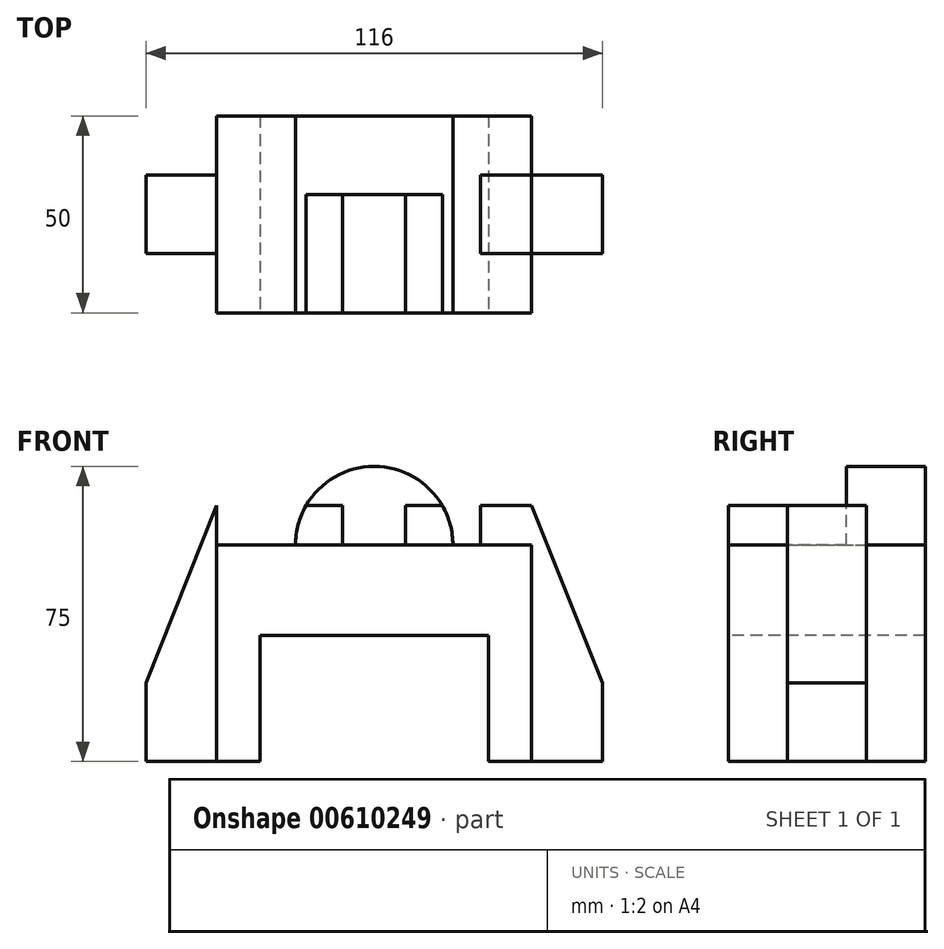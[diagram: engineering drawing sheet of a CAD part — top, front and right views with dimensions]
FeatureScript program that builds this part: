
annotation { "Feature Type Name" : "Feature", "Feature Type Description" : "" }
export const myFeature = defineFeature(function(context is Context, id is Id, definition is map)
    precondition{}
    {
        {
            var Q0;
            Q0=qCreatedBy(makeId("Top.planeOp"),FACE);
            var sketch = newSketch(context, id + "F0", { "sketchPlane" : qUnion([Q0])});
            skLineSegment(sketch, "E0.bottom", {"start": v(40, 25) * mm, "end": v(-40, 25) * mm});
            skLineSegment(sketch, "E0.top", {"start": v(40, -25) * mm, "end": v(-40, -25) * mm});
            skLineSegment(sketch, "E0.left", {"start": v(40, 25) * mm, "end": v(40, -25) * mm});
            skLineSegment(sketch, "E0.right", {"start": v(-40, 25) * mm, "end": v(-40, -25) * mm});
            skPoint(sketch, "E0.middle", {"position": v(0, 0) * mm});
            skSolve(sketch);
        }
        {
            var Q0;
            Q0 = qSketchRegion(id + "F0", true);
            extrude(context, id + "F1", {"entities" : qUnion([Q0]), "depth" : 55 * mm, "offsetDistance" : 25 * mm});
        }
        {
            var Q0;
            Q0=makeQuery(id+"F1.opExtrude","SWEPT_FACE",FACE,{"disambiguationData":[OSD([sQuery(id+"F0.wireOp",EDGE,"E0.top")])]});
            var sketch = newSketch(context, id + "F2", { "sketchPlane" : qUnion([Q0])});
            skLineSegment(sketch, "E1", {"start": v(-40, 0) * mm, "end": v(-29, 0) * mm});
            skLineSegment(sketch, "E2", {"start": v(40, 0) * mm, "end": v(29, 0) * mm});
            skLineSegment(sketch, "E3", {"start": v(29, 0) * mm, "end": v(29, 32) * mm});
            skLineSegment(sketch, "E4", {"start": v(29, 32) * mm, "end": v(-29, 32) * mm});
            skLineSegment(sketch, "E5", {"start": v(-29, 32) * mm, "end": v(-29, 0) * mm});
            skSolve(sketch);
        }
        {
            var Q0;
            {var subQ0=sQuery(id+"F2.wireOp",EDGE,"E3");Q0=makeQuery(id+"F2.imprint","IMPRINT",FACE,{"disambiguationData":[TD([[makeQuery(id+"F2.imprint","IMPRINT",EDGE,{"derivedFrom":subQ0}),1.0]])]});}
            extrude(context, id + "F3", {"entities" : qUnion([Q0]), "operationType" : NewBodyOperationType.REMOVE, "oppositeDirection" : true, "depth" : 114.9 * mm, "offsetDistance" : 25 * mm});
        }
        {
            var Q0;
            {var subQ0=sQuery(id+"F0.wireOp",EDGE,"E0.bottom");var subQ1=makeQuery(id+"F1.opExtrude","CAP_EDGE",EDGE,{"disambiguationData":[OSD([subQ0])],"isStart":false});Q0=makeQuery(id+"FYNZewFaTHs3g9M_1.boolean.opBoolean","MERGE",FACE,{"derivedFrom":[makeQuery(id+"F1.opExtrude","SWEPT_FACE",FACE,{"disambiguationData":[OSD([subQ0])]}),makeQuery(id+"FYNZewFaTHs3g9M_1.opExtrude","SWEPT_FACE",FACE,{"disambiguationData":[OSD([subQ0]),TDD([makeQuery(id+"F5iMfnjMPppVyk3_1.imprint","IMPRINT",EDGE,{"disambiguationData":[TD([[makeQuery(id+"F5iMfnjMPppVyk3_1.imprint","INTERSECT",VERTEX,{"derivedFrom":[subQ1,sQuery(id+"F5iMfnjMPppVyk3_1.wireOp",EDGE,"3RxKEA0C-GHss-9lNF-Rws6-FtL8dP0ttHGj")]}),1.0]])],"derivedFrom":subQ1})])]}),makeQuery(id+"FYNZewFaTHs3g9M_1.opExtrude","SWEPT_FACE",FACE,{"disambiguationData":[OSD([subQ0]),TDD([makeQuery(id+"F5iMfnjMPppVyk3_1.imprint","IMPRINT",EDGE,{"disambiguationData":[TD([[makeQuery(id+"F5iMfnjMPppVyk3_1.imprint","INTERSECT",VERTEX,{"derivedFrom":[subQ1,sQuery(id+"F5iMfnjMPppVyk3_1.wireOp",EDGE,"J8qmjmCr-zK4k-0Xos-QoFt-C1XgcybPVIlB")]}),1.0]])],"derivedFrom":subQ1})])]})]});}
            var sketch = newSketch(context, id + "F4", { "sketchPlane" : qUnion([Q0])});
            skArc(sketch, "E6", {"start": v(20, 55) * mm, "mid": v(0, 75) * mm, "end": v(-20, 55) * mm});
            skLineSegment(sketch, "E7", {"start": v(0, 55) * mm, "end": v(0, 55) * mm});
            skSolve(sketch);
        }
        {
            var Q0;
            Q0 = qSketchRegion(id + "F4", true);
            var Q1;
            {var subQ0=sQuery(id+"F4.wireOp",EDGE,"E6");Q1=makeQuery(id+"F4.imprint","IMPRINT",FACE,{"disambiguationData":[TD([[makeQuery(id+"F4.imprint","IMPRINT",EDGE,{"derivedFrom":subQ0}),1.0]])]});}
            var Q2;
            Q2=makeQuery(id+"F1.opExtrude","SWEPT_FACE",FACE,{"disambiguationData":[OSD([sQuery(id+"F0.wireOp",EDGE,"E0.top")])]});
            extrude(context, id + "F5", {"entities" : qUnion([Q0, Q1]), "endBound" : BoundingType.UP_TO_SURFACE, "oppositeDirection" : true, "depth" : 20 * mm, "endBoundEntityFace" : qUnion([Q2]), "offsetDistance" : 25 * mm});
        }
        {
            var Q0;
            Q0=makeQuery(id+"F5.opExtrude","CAP_FACE",FACE,{"disambiguationData":[OSD([sQuery(id+"F0.wireOp",EDGE,"E0.bottom"),sQuery(id+"F4.wireOp",EDGE,"E6")])],"isStart":false});
            var sketch = newSketch(context, id + "F6", { "sketchPlane" : qUnion([Q0])});
            skLineSegment(sketch, "E8", {"start": v(0, 55) * mm, "end": v(-8, 55) * mm});
            skLineSegment(sketch, "E9", {"start": v(-8, 55) * mm, "end": v(8, 55) * mm});
            skLineSegment(sketch, "E10", {"start": v(8, 55) * mm, "end": v(8, 65) * mm});
            skLineSegment(sketch, "E11", {"start": v(8, 65) * mm, "end": v(17.32, 65) * mm});
            skLineSegment(sketch, "E12", {"start": v(-8, 55) * mm, "end": v(-8, 65) * mm});
            skLineSegment(sketch, "E13", {"start": v(-8, 65) * mm, "end": v(-17.32, 65) * mm});
            skLineSegment(sketch, "E14", {"start": v(-8, 65) * mm, "end": v(8, 65) * mm});
            skSolve(sketch);
        }
        {
            var Q0;
            {var subQ0=sQuery(id+"F6.wireOp",EDGE,"E10");Q0=makeQuery(id+"F6.imprint","IMPRINT",FACE,{"disambiguationData":[TD([[makeQuery(id+"F6.imprint","IMPRINT",EDGE,{"derivedFrom":subQ0}),1.0]])]});}
            extrude(context, id + "F7", {"entities" : qUnion([Q0]), "operationType" : NewBodyOperationType.REMOVE, "oppositeDirection" : true, "depth" : 30 * mm, "offsetDistance" : 25 * mm});
        }
        {
            var Q0;
            {var subQ0=sQuery(id+"F6.wireOp",EDGE,"E11");Q0=makeQuery(id+"F6.imprint","IMPRINT",FACE,{"disambiguationData":[TD([[makeQuery(id+"F6.imprint","IMPRINT",EDGE,{"derivedFrom":subQ0}),1.0]])]});}
            extrude(context, id + "F8", {"entities" : qUnion([Q0]), "operationType" : NewBodyOperationType.REMOVE, "oppositeDirection" : true, "depth" : 30 * mm, "offsetDistance" : 25 * mm});
        }
        {
            var Q0;
            Q0=qCreatedBy(makeId("Front.planeOp"),FACE);
            var sketch = newSketch(context, id + "F9", { "sketchPlane" : qUnion([Q0])});
            skLineSegment(sketch, "E15.0.0", {"start": v(-29, 0) * mm, "end": v(-29, 32) * mm});
            skLineSegment(sketch, "E15.0.1", {"start": v(-29, 32) * mm, "end": v(29, 32) * mm});
            skLineSegment(sketch, "E15.0.2", {"start": v(29, 32) * mm, "end": v(29, 0) * mm});
            skLineSegment(sketch, "E15.0.3", {"start": v(29, 0) * mm, "end": v(40, 0) * mm});
            skLineSegment(sketch, "E15.0.4", {"start": v(40, 0) * mm, "end": v(40, 55) * mm});
            skLineSegment(sketch, "E15.0.5", {"start": v(40, 55) * mm, "end": v(-40, 55) * mm});
            skLineSegment(sketch, "E15.0.6", {"start": v(-40, 55) * mm, "end": v(-40, 0) * mm});
            skLineSegment(sketch, "E15.0.7", {"start": v(-40, 0) * mm, "end": v(-29, 0) * mm});
            skLineSegment(sketch, "E16.bottom", {"start": v(-40, 0) * mm, "end": v(-58, 0) * mm});
            skLineSegment(sketch, "E16.top", {"start": v(-40, 65) * mm, "end": v(-58, 65) * mm});
            skLineSegment(sketch, "E16.left", {"start": v(-40, 0) * mm, "end": v(-40, 65) * mm});
            skLineSegment(sketch, "E16.right", {"start": v(-58, 0) * mm, "end": v(-58, 65) * mm});
            skLineSegment(sketch, "E17", {"start": v(-58, 0) * mm, "end": v(-58, 20) * mm});
            skLineSegment(sketch, "E18", {"start": v(-40, 55) * mm, "end": v(-27, 55) * mm});
            skLineSegment(sketch, "E19", {"start": v(-27, 55) * mm, "end": v(-27, 65) * mm});
            skLineSegment(sketch, "E20", {"start": v(-27, 65) * mm, "end": v(-40, 65) * mm});
            skLineSegment(sketch, "E21", {"start": v(-58, 20) * mm, "end": v(-40, 65) * mm});
            skLineSegment(sketch, "E22.MirrorCS", {"start": v(40, 0) * mm, "end": v(40, 65) * mm});
            skLineSegment(sketch, "E23.MirrorCS", {"start": v(58, 20) * mm, "end": v(40, 65) * mm});
            skLineSegment(sketch, "E24.MirrorCS", {"start": v(58, 0) * mm, "end": v(58, 20) * mm});
            skLineSegment(sketch, "E25.MirrorCS", {"start": v(40, 0) * mm, "end": v(58, 0) * mm});
            skLineSegment(sketch, "E26.MirrorCS", {"start": v(27, 65) * mm, "end": v(40, 65) * mm});
            skLineSegment(sketch, "E27.MirrorCS", {"start": v(27, 55) * mm, "end": v(27, 65) * mm});
            skSolve(sketch);
        }
        {
            var Q0;
            {var subQ3=sQuery(id+"F9.wireOp",EDGE,"E16.bottom");Q0=makeQuery(id+"F9.imprint","IMPRINT",FACE,{"disambiguationData":[TD([[makeQuery(id+"F9.imprint","IMPRINT",EDGE,{"derivedFrom":subQ3}),-1.0]])]});}
            var Q1;
            {var subQ2=sQuery(id+"F9.wireOp",EDGE,"E18");Q1=makeQuery(id+"F9.imprint","IMPRINT",FACE,{"disambiguationData":[TD([[makeQuery(id+"F9.imprint","IMPRINT",EDGE,{"derivedFrom":subQ2}),1.0]])]});}
            var Q2;
            {var subQ0=sQuery(id+"F9.wireOp",EDGE,"E23.MirrorCS");Q2=makeQuery(id+"F9.imprint","IMPRINT",FACE,{"disambiguationData":[TD([[makeQuery(id+"F9.imprint","IMPRINT",EDGE,{"derivedFrom":subQ0}),1.0]])]});}
            var Q3;
            {var subQ4=sQuery(id+"F9.wireOp",EDGE,"E26.MirrorCS");Q3=makeQuery(id+"F9.imprint","IMPRINT",FACE,{"disambiguationData":[TD([[makeQuery(id+"F9.imprint","IMPRINT",EDGE,{"derivedFrom":subQ4}),-1.0]])]});}
            extrude(context, id + "F10", {"entities" : qUnion([Q0, Q1, Q2, Q3]), "operationType" : NewBodyOperationType.ADD, "depth" : 10 * mm, "offsetDistance" : 25 * mm, "hasSecondDirection" : true, "secondDirectionOppositeDirection" : true, "secondDirectionDepth" : 10 * mm});
        }
    });
